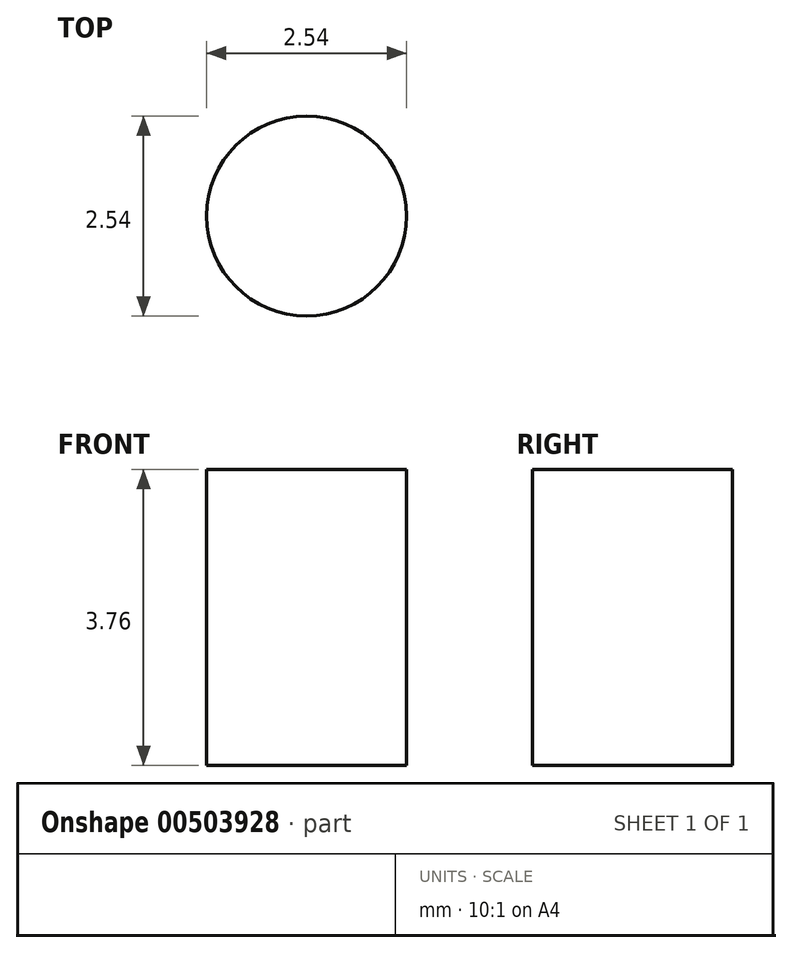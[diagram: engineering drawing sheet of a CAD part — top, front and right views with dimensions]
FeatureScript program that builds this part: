
annotation { "Feature Type Name" : "Feature", "Feature Type Description" : "" }
export const myFeature = defineFeature(function(context is Context, id is Id, definition is map)
    precondition{}
    {
        {
            var Q0;
            Q0=qCreatedBy(makeId("Top.planeOp"),FACE);
            var sketch = newSketch(context, id + "F0", { "sketchPlane" : qUnion([Q0])});
            skCircle(sketch, "E0", {"center": v(0, 0) * mm, "radius": 1.27 * mm});
            skSolve(sketch);
        }
        {
            var Q0;
            Q0=makeQuery(id+"F0.imprint","IMPRINT",FACE,{"disambiguationData":[TD([[makeQuery(id+"F0.imprint","IMPRINT",EDGE,{"derivedFrom":sQuery(id+"F0.wireOp",EDGE,"E0")}),1.0]])]});
            extrude(context, id + "F1", {"entities" : qUnion([Q0]), "depth" : 3.76 * mm});
        }
    });
